# Revit family: Aluco Skylight Therm (en)
name_source: partatom
category: Generic Models
units: mm (PartAtom-declared; Revit-internal decimal feet)

## family parameters
Always vertical = No
Can host rebar = No
Cut with Voids When Loaded = No
OmniClass Number = 23.30.30.00
OmniClass Title = Skylights
Part Type = Normal
Room Calculation Point = No
Round Connector Dimension = Use Diameter
Shared = No
Work Plane-Based = Yes

## types (1)
- Aluco Skylight Therm (en)
    Base material = Aluco - galvanized steel
    Breaking load resistance = UL 2500
    Compressive load resistance = DL 2500
    Default Elevation = 0 mm  [stored 0 ft]
    Description = Continuous skylights made in accordance with the requirements of PN-EN14963: 2006, with CE marking
    Fire protection class = BRoof (t1)
    IfcExportAs = "IfcWindowType"
    Manufacturer = ALUCO SYSTEM SP. Z O.O
    Model = Skylight Therm
    Panel material = Aluco - polycarbonate
    Product URL = https://aluco.com.pl
    Profile material = Aluco - aluminum
    Safety classification against drop from height = SB 1200
    Type Comments = Barrel vault continuous skylights
    Type Image = ALUCO SKYLIGHT SL.png
    URL = https://aluco.com.pl

note: [stored X ft] marks values corroborated as IEEE doubles in the binary element streams (Revit-internal decimal feet)
